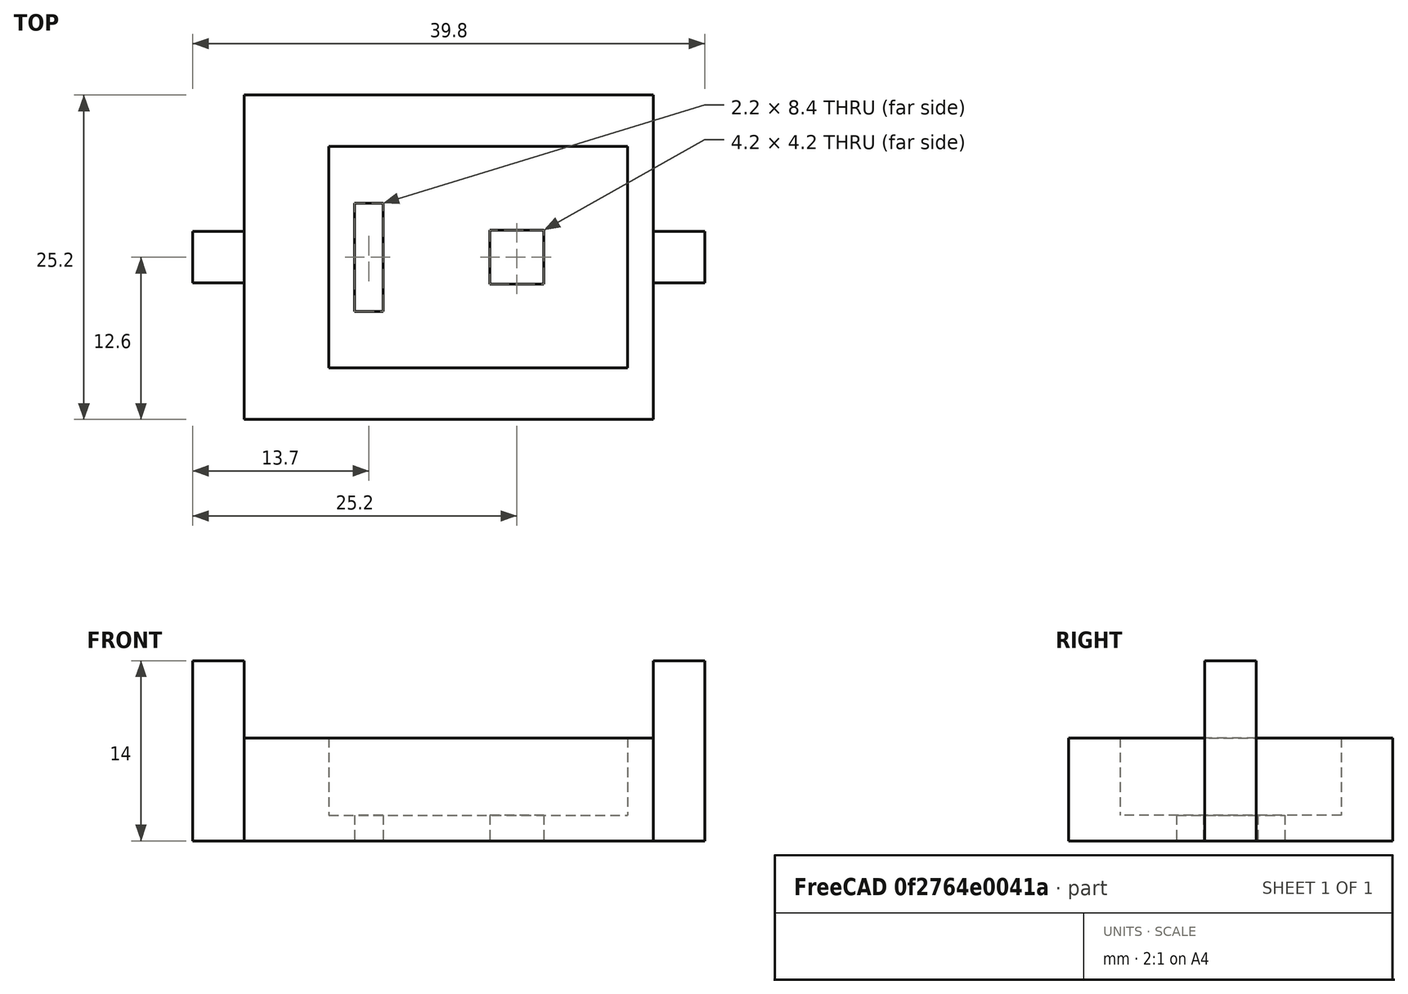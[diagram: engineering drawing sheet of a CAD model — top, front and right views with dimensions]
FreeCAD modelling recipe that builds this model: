
FCSTD DOCUMENT  (FreeCAD 0.18.1R)
Label: HeadCYL
License: All rights reserved
LicenseURL: http://en.wikipedia.org/wiki/All_rights_reserved
objects: TechDraw::DrawViewDimension×13, Sketcher::SketchObject×9, TechDraw::DrawProjGroupItem×4, PartDesign::Pad×3, PartDesign::Plane×3, PartDesign::Pocket×3, TechDraw::DrawSVGTemplate×2, TechDraw::DrawPage×2, PartDesign::Body×1, TechDraw::DrawViewPart×1, TechDraw::DrawProjGroup×1
note: 25 computed .brp shape members not serialized (recipe doc carries the construction recipe); baked Part::Feature solids carry a one-line shape summary decoded from their .brp

FEATURE [Sketcher::SketchObject] Sketch
  MapMode = 5
  Support = -> [XY_Plane]
  sketch-geometry (12):
    g0: LineSegment StartX=-4 StartY=14.6 StartZ=0 EndX=-4 EndY=10.6 EndZ=0
    g1: LineSegment StartX=-4 StartY=10.6 StartZ=0 EndX=0 EndY=10.6 EndZ=0
    g2: LineSegment StartX=0 StartY=10.6 StartZ=0 EndX=0 EndY=0 EndZ=0
    g3: LineSegment StartX=0 StartY=0 StartZ=0 EndX=31.8 EndY=0 EndZ=0
    g4: LineSegment StartX=31.8 StartY=0 StartZ=0 EndX=31.8 EndY=10.6 EndZ=0
    g5: LineSegment StartX=31.8 StartY=10.6 StartZ=0 EndX=35.8 EndY=10.6 EndZ=0
    g6: LineSegment StartX=35.8 StartY=10.6 StartZ=0 EndX=35.8 EndY=14.6 EndZ=0
    g7: LineSegment StartX=35.8 StartY=14.6 StartZ=0 EndX=31.8 EndY=14.6 EndZ=0
    g8: LineSegment StartX=31.8 StartY=14.6 StartZ=0 EndX=31.8 EndY=25.2 EndZ=0
    g9: LineSegment StartX=31.8 StartY=25.2 StartZ=0 EndX=0 EndY=25.2 EndZ=0
    g10: LineSegment StartX=0 StartY=25.2 StartZ=0 EndX=0 EndY=14.6 EndZ=0
    g11: LineSegment StartX=0 StartY=14.6 StartZ=0 EndX=-4 EndY=14.6 EndZ=0
  constraints (35):
    c: Coincident(g0,g1)
    c: Coincident(g1,g2)
    c: Coincident(g2,g3)
    c: Coincident(g3,g4)
    c: Coincident(g4,g5)
    c: Coincident(g5,g6)
    c: Coincident(g6,g7)
    c: Coincident(g7,g8)
    c: Coincident(g8,g9)
    c: Coincident(g9,g10)
    c: Coincident(g10,g11)
    c: Coincident(g11,g0)
    c: Vertical(g0)
    c: Vertical(g6)
    c: Vertical(g10)
    c: Vertical(g8)
    c: Vertical(g2)
    c: Vertical(g4)
    c: Horizontal(g11)
    c: Horizontal(g1)
    c: Horizontal(g3)
    c: Horizontal(g9)
    c: Horizontal(g7)
    c: Horizontal(g5)
    c: DistanceX(g3,g3) = 31.8
    c: Coincident(g2,g-1)
    c: DistanceY(g2,g2) = 10.6
    c: DistanceY(g10,g10) = 10.6
    c: DistanceY(g8,g8) = 10.6
    c: DistanceY(g4,g4) = 10.6
    c: DistanceX(g11,g11) = 4
    c: Equal(g11,g7)
    c: Equal(g7,g5)
    c: Equal(g5,g1)
    c: DistanceY(g0,g0) = 4
FEATURE [PartDesign::Pad] Pad
  Length = 8
  Length2 = 100
  Profile = -> Sketch
  Type = 0
FEATURE [PartDesign::Plane] DatumPlane
  Length = 53.8303
  MapMode = 5
  Placement = pos=(0,0,8) rot=(0,0,1;0rad)
  ResizeMode = 0
  Support = -> [Pad]
  Width = 43.2303
FEATURE [Sketcher::SketchObject] Sketch001
  MapMode = 5
  Placement = pos=(0,0,8) rot=(0,0,1;0rad)
  Support = -> [DatumPlane]
  sketch-geometry (4):
    g0: LineSegment StartX=3.91455 StartY=22.072 StartZ=0 EndX=27.1145 EndY=22.072 EndZ=0
    g1: LineSegment StartX=27.1145 StartY=22.072 StartZ=0 EndX=27.1145 EndY=4.87202 EndZ=0
    g2: LineSegment StartX=27.1145 StartY=4.87202 StartZ=0 EndX=3.91455 EndY=4.87202 EndZ=0
    g3: LineSegment StartX=3.91455 StartY=4.87202 StartZ=0 EndX=3.91455 EndY=22.072 EndZ=0
  constraints (10):
    c: Coincident(g0,g1)
    c: Coincident(g1,g2)
    c: Coincident(g2,g3)
    c: Coincident(g3,g0)
    c: Horizontal(g0)
    c: Horizontal(g2)
    c: Vertical(g1)
    c: Vertical(g3)
    c: DistanceX(g0,g0) = 23.2
    c: DistanceY(g3,g3) = 17.2
FEATURE [Sketcher::SketchObject] Sketch002
  MapMode = 5
  Placement = pos=(0,0,8) rot=(0,0,1;0rad)
  Support = -> [DatumPlane]
  sketch-geometry (4):
    g0: LineSegment StartX=2.87872 StartY=21.6787 StartZ=0 EndX=26.0787 EndY=21.6787 EndZ=0
    g1: LineSegment StartX=26.0787 StartY=21.6787 StartZ=0 EndX=26.0787 EndY=4.47867 EndZ=0
    g2: LineSegment StartX=26.0787 StartY=4.47867 StartZ=0 EndX=2.87872 EndY=4.47867 EndZ=0
    g3: LineSegment StartX=2.87872 StartY=4.47867 StartZ=0 EndX=2.87872 EndY=21.6787 EndZ=0
  constraints (10):
    c: Coincident(g0,g1)
    c: Coincident(g1,g2)
    c: Coincident(g2,g3)
    c: Coincident(g3,g0)
    c: Horizontal(g0)
    c: Horizontal(g2)
    c: Vertical(g1)
    c: Vertical(g3)
    c: DistanceX(g0,g0) = 23.2
    c: DistanceY(g3,g3) = 17.2
FEATURE [Sketcher::SketchObject] Sketch003
  MapMode = 5
  Placement = pos=(0,0,8) rot=(0,0,1;0rad)
  Support = -> [DatumPlane]
  sketch-geometry (4):
    g0: LineSegment StartX=6.6 StartY=21.2 StartZ=0 EndX=29.8 EndY=21.2 EndZ=0
    g1: LineSegment StartX=29.8 StartY=21.2 StartZ=0 EndX=29.8 EndY=4 EndZ=0
    g2: LineSegment StartX=29.8 StartY=4 StartZ=0 EndX=6.6 EndY=4 EndZ=0
    g3: LineSegment StartX=6.6 StartY=4 StartZ=0 EndX=6.6 EndY=21.2 EndZ=0
  constraints (12):
    c: Coincident(g0,g1)
    c: Coincident(g1,g2)
    c: Coincident(g2,g3)
    c: Coincident(g3,g0)
    c: Horizontal(g0)
    c: Horizontal(g2)
    c: Vertical(g1)
    c: Vertical(g3)
    c: DistanceX(g-1,g2) = 6.6
    c: DistanceX(g2,g2) = 23.2
    c: DistanceY(g3,g3) = 17.2
    c: DistanceY(g-1,g2) = 4
FEATURE [PartDesign::Pocket] Pocket
  BaseFeature = -> Pad
  Length = 6
  Length2 = 100
  Profile = -> Sketch003
  Type = 0
FEATURE [Sketcher::SketchObject] Sketch004
  MapMode = 5
  Placement = pos=(0,0,2) rot=(0,0,1;0rad)
  Support = -> [Pocket]
FEATURE [PartDesign::Plane] DatumPlane001
  Length = 53.8303
  MapMode = 5
  Placement = pos=(0,0,2) rot=(0,0,1;0rad)
  ResizeMode = 0
  Support = -> [Pocket]
  Width = 43.2303
FEATURE [Sketcher::SketchObject] Sketch005
  MapMode = 5
  Placement = pos=(0,0,2) rot=(0,0,1;0rad)
  Support = -> [DatumPlane001]
  sketch-geometry (4):
    g0: LineSegment StartX=8.6 StartY=16.8 StartZ=0 EndX=10.8 EndY=16.8 EndZ=0
    g1: LineSegment StartX=10.8 StartY=16.8 StartZ=0 EndX=10.8 EndY=8.4 EndZ=0
    g2: LineSegment StartX=10.8 StartY=8.4 StartZ=0 EndX=8.6 EndY=8.4 EndZ=0
    g3: LineSegment StartX=8.6 StartY=8.4 StartZ=0 EndX=8.6 EndY=16.8 EndZ=0
  constraints (12):
    c: Coincident(g0,g1)
    c: Coincident(g1,g2)
    c: Coincident(g2,g3)
    c: Coincident(g3,g0)
    c: Horizontal(g0)
    c: Horizontal(g2)
    c: Vertical(g1)
    c: Vertical(g3)
    c: DistanceY(g3,g3) = 8.4
    c: DistanceX(g0,g0) = 2.2
    c: DistanceY(g-1,g2) = 8.4
    c: DistanceX(g-1,g2) = 8.6
FEATURE [PartDesign::Pocket] Pocket001
  BaseFeature = -> Pocket
  Length = 7
  Length2 = 100
  Profile = -> Sketch005
  Type = 0
FEATURE [Sketcher::SketchObject] Sketch006
  MapMode = 5
  Placement = pos=(0,0,2) rot=(0,0,1;0rad)
  Support = -> [DatumPlane001]
  sketch-geometry (4):
    g0: LineSegment StartX=19.1 StartY=14.7 StartZ=0 EndX=23.3 EndY=14.7 EndZ=0
    g1: LineSegment StartX=23.3 StartY=14.7 StartZ=0 EndX=23.3 EndY=10.5 EndZ=0
    g2: LineSegment StartX=23.3 StartY=10.5 StartZ=0 EndX=19.1 EndY=10.5 EndZ=0
    g3: LineSegment StartX=19.1 StartY=10.5 StartZ=0 EndX=19.1 EndY=14.7 EndZ=0
  constraints (12):
    c: Coincident(g0,g1)
    c: Coincident(g1,g2)
    c: Coincident(g2,g3)
    c: Coincident(g3,g0)
    c: Horizontal(g0)
    c: Horizontal(g2)
    c: Vertical(g1)
    c: Vertical(g3)
    c: DistanceX(g0,g0) = 4.2
    c: Equal(g3,g0)
    c: DistanceY(g-1,g2) = 10.5
    c: DistanceX(g-1,g2) = 19.1
FEATURE [PartDesign::Pocket] Pocket002
  BaseFeature = -> Pocket001
  Length = 5
  Length2 = 100
  Profile = -> Sketch006
  Type = 0
FEATURE [PartDesign::Plane] DatumPlane002
  Length = 53.8303
  MapMode = 5
  Placement = pos=(0,0,8) rot=(0,0,1;0rad)
  ResizeMode = 0
  Support = -> [Pocket002]
  Width = 43.2303
FEATURE [Sketcher::SketchObject] Sketch007
  MapMode = 5
  Placement = pos=(0,0,8) rot=(0,0,1;0rad)
  Support = -> [DatumPlane002]
  sketch-geometry (4):
    g0: LineSegment StartX=-4 StartY=14.6 StartZ=0 EndX=0 EndY=14.6 EndZ=0
    g1: LineSegment StartX=0 StartY=14.6 StartZ=0 EndX=0 EndY=10.6 EndZ=0
    g2: LineSegment StartX=0 StartY=10.6 StartZ=0 EndX=-4 EndY=10.6 EndZ=0
    g3: LineSegment StartX=-4 StartY=10.6 StartZ=0 EndX=-4 EndY=14.6 EndZ=0
  constraints (12):
    c: Coincident(g0,g1)
    c: Coincident(g1,g2)
    c: Coincident(g2,g3)
    c: Coincident(g3,g0)
    c: Horizontal(g0)
    c: Horizontal(g2)
    c: Vertical(g1)
    c: Vertical(g3)
    c: DistanceX(g0,g0) = 4
    c: DistanceY(g3,g3) = 4
    c: DistanceX(g-1,g1) = 0
    c: DistanceY(g-1,g1) = 10.6
FEATURE [PartDesign::Pad] Pad001
  BaseFeature = -> Pocket002
  Length = 6
  Length2 = 100
  Profile = -> Sketch007
  Type = 0
FEATURE [Sketcher::SketchObject] Sketch008
  MapMode = 5
  Placement = pos=(0,0,8) rot=(0,0,1;0rad)
  Support = -> [DatumPlane002]
  sketch-geometry (4):
    g0: LineSegment StartX=31.8 StartY=14.6 StartZ=0 EndX=35.8 EndY=14.6 EndZ=0
    g1: LineSegment StartX=35.8 StartY=14.6 StartZ=0 EndX=35.8 EndY=10.6 EndZ=0
    g2: LineSegment StartX=35.8 StartY=10.6 StartZ=0 EndX=31.8 EndY=10.6 EndZ=0
    g3: LineSegment StartX=31.8 StartY=10.6 StartZ=0 EndX=31.8 EndY=14.6 EndZ=0
  constraints (12):
    c: Coincident(g0,g1)
    c: Coincident(g1,g2)
    c: Coincident(g2,g3)
    c: Coincident(g3,g0)
    c: Horizontal(g0)
    c: Horizontal(g2)
    c: Vertical(g1)
    c: Vertical(g3)
    c: DistanceX(g0,g0) = 4
    c: DistanceY(g3,g3) = 4
    c: DistanceX(g-1,g2) = 31.8
    c: DistanceY(g-1,g2) = 10.6
FEATURE [PartDesign::Pad] Pad002
  BaseFeature = -> Pad001
  Length = 6
  Length2 = 100
  Profile = -> Sketch008
  Type = 0
FEATURE [PartDesign::Body] Body
  Group = -> [Sketch,Pad,DatumPlane,Sketch001,Sketch002,Sketch003,Pocket,Sketch004,DatumPlane001,Sketch005,Pocket001,Sketch006,Pocket002,DatumPlane002,Sketch007,Pad001,Sketch008,Pad002]
  Origin = -> Origin
  Tip = -> Pad002
FEATURE [TechDraw::DrawSVGTemplate] Template
  EditableTexts = Designed_by_Name=Designed by Name; Drawing_number=Drawing number; FC-Date=Date; FC-SC=Scale; FC-SH=Sheet; FC-Title=Title; Subtitle=Subtitle; Weight=Weight
  Height = 210
  Orientation = 1
  Width = 297
FEATURE [TechDraw::DrawViewPart] View
  CoarseView = false
  Direction = (0,-1,0)
  Focus = 100
  HardHidden = false
  IsoCount = 0
  IsoHidden = false
  IsoVisible = false
  LockPosition = false
  Perspective = false
  Rotation = 0
  ScaleType = 0
  SeamHidden = false
  SeamVisible = false
  SmoothHidden = false
  SmoothVisible = false
  Source = -> [Body]
  X = 148.5
  Y = 105
FEATURE [TechDraw::DrawPage] Page
  KeepUpdated = true
  ProjectionType = 0
  Template = -> Template
  Views = -> [View]
FEATURE [TechDraw::DrawSVGTemplate] Template001
  EditableTexts = Approved1=Approved 1; Approved2=Approved 2; CheckedBy=Checked By; Code=Code; CompanyAddress=1234 Main St; CompanyName=Company Name; DrawingNumber=Drawing Number; DrawingTitle1=Drawing Title 1; DrawingTitle2=Drawing Title 2; DrawingTitle3=Drawing Title 3; DrawnBy=Drawn By; Revision=Rev; Scale=Scale; Sheet=Sheet n of m; Weight=Weight
  Height = 279.4
  Orientation = 1
  Width = 431.8
FEATURE [TechDraw::DrawProjGroupItem] ProjItem  label="Front"
  CoarseView = false
  Direction = (0,-1,0)
  Focus = 100
  HardHidden = false
  IsoCount = 0
  IsoHidden = false
  IsoVisible = false
  LockPosition = true
  Perspective = false
  Rotation = 0
  RotationVector = (1,0,0)
  Scale = 2
  ScaleType = 2
  SeamHidden = false
  SeamVisible = false
  SmoothHidden = false
  SmoothVisible = false
  Source = -> [Body]
  Type = 0
  X = 0
  Y = 0
FEATURE [TechDraw::DrawProjGroupItem] ProjItem001  label="Left"
  CoarseView = false
  Direction = (-1,-1e-16,0)
  Focus = 100
  HardHidden = false
  IsoCount = 0
  IsoHidden = false
  IsoVisible = false
  LockPosition = false
  Perspective = false
  Rotation = 0
  RotationVector = (1e-16,-1,0)
  Scale = 2
  ScaleType = 2
  SeamHidden = false
  SeamVisible = false
  SmoothHidden = false
  SmoothVisible = false
  Source = -> [Body]
  Type = 1
  X = 95.6102
  Y = 0
FEATURE [TechDraw::DrawProjGroupItem] ProjItem002  label="FrontTopLeft"
  CoarseView = false
  Direction = (-1,-1,1)
  Focus = 100
  HardHidden = false
  IsoCount = 0
  IsoHidden = false
  IsoVisible = false
  LockPosition = false
  Perspective = false
  Rotation = 0
  RotationVector = (1,-1,0)
  Scale = 2
  ScaleType = 2
  SeamHidden = false
  SeamVisible = false
  SmoothHidden = false
  SmoothVisible = false
  Source = -> [Body]
  Type = 6
  X = 95.6102
  Y = -95.6102
FEATURE [TechDraw::DrawProjGroupItem] ProjItem003  label="Top"
  CoarseView = false
  Direction = (0,0,1)
  Focus = 100
  HardHidden = false
  IsoCount = 0
  IsoHidden = false
  IsoVisible = false
  LockPosition = false
  Perspective = false
  Rotation = 0
  RotationVector = (1,0,0)
  Scale = 2
  ScaleType = 2
  SeamHidden = false
  SeamVisible = false
  SmoothHidden = false
  SmoothVisible = false
  Source = -> [Body]
  Type = 4
  X = 0
  Y = -95.6102
FEATURE [TechDraw::DrawProjGroup] ProjGroup
  Anchor = -> ProjItem
  AutoDistribute = true
  LockPosition = false
  ProjectionType = 0
  Rotation = 0
  Scale = 2
  ScaleType = 2
  Source = -> [Body]
  Views = -> [ProjItem,ProjItem001,ProjItem002,ProjItem003]
  X = 98.093
  Y = 193.436
  spacingX = 15
  spacingY = 15
FEATURE [TechDraw::DrawViewDimension] Dimension
  Arbitrary = false
  FormatSpec = %.4f
  LockPosition = false
  MeasureType = 1
  OverTolerance = 0
  References2D = -> [ProjItem]
  Rotation = 0
  ScaleType = 0
  Type = 1
  UnderTolerance = 0
  X = 1.24312
  Y = -26.4312
FEATURE [TechDraw::DrawViewDimension] Dimension001
  Arbitrary = false
  FormatSpec = %.4f
  LockPosition = false
  MeasureType = 1
  OverTolerance = 0
  References2D = -> [ProjItem]
  Rotation = 0
  ScaleType = 0
  Type = 1
  UnderTolerance = 0
  X = -34.8677
  Y = 25.8097
FEATURE [TechDraw::DrawViewDimension] Dimension002
  Arbitrary = false
  FormatSpec = %.4f
  LockPosition = false
  MeasureType = 1
  OverTolerance = 0
  References2D = -> [ProjItem]
  Rotation = 0
  ScaleType = 0
  Type = 2
  UnderTolerance = 0
  X = -51.2989
  Y = -1.24312
FEATURE [TechDraw::DrawViewDimension] Dimension003
  Arbitrary = false
  FormatSpec = %.4f
  LockPosition = false
  MeasureType = 1
  OverTolerance = 0
  References2D = -> [ProjItem001]
  Rotation = 0
  ScaleType = 0
  Type = 1
  UnderTolerance = 0
  X = 0
  Y = -25.1881
FEATURE [TechDraw::DrawViewDimension] Dimension004
  Arbitrary = false
  FormatSpec = %.4f
  LockPosition = false
  MeasureType = 1
  OverTolerance = 0
  References2D = -> [ProjItem001]
  Rotation = 0
  ScaleType = 0
  Type = 1
  UnderTolerance = 0
  X = 1.86468
  Y = 25.8097
FEATURE [TechDraw::DrawViewDimension] Dimension005
  Arbitrary = false
  FormatSpec = %.4f
  LockPosition = false
  MeasureType = 1
  OverTolerance = 0
  References2D = -> [ProjItem001]
  Rotation = 0
  ScaleType = 0
  Type = 2
  UnderTolerance = 0
  X = 35.4558
  Y = -6.62156
FEATURE [TechDraw::DrawViewDimension] Dimension006
  Arbitrary = false
  FormatSpec = %.4f
  LockPosition = false
  MeasureType = 1
  OverTolerance = 0
  References2D = -> [ProjItem003]
  Rotation = 0
  ScaleType = 0
  Type = 1
  UnderTolerance = 0
  X = -0.310781
  Y = 40.4283
FEATURE [TechDraw::DrawViewDimension] Dimension007
  Arbitrary = false
  FormatSpec = %.4f
  LockPosition = false
  MeasureType = 1
  OverTolerance = 0
  References2D = -> [ProjItem003]
  Rotation = 0
  ScaleType = 0
  Type = 2
  UnderTolerance = 0
  X = -47.8803
  Y = -0.310781
FEATURE [TechDraw::DrawViewDimension] Dimension008
  Arbitrary = false
  FormatSpec = %.4f
  LockPosition = false
  MeasureType = 1
  OverTolerance = 0
  References2D = -> [ProjItem003]
  Rotation = 0
  ScaleType = 0
  Type = 2
  UnderTolerance = 0
  X = -53.8654
  Y = -0.932342
FEATURE [TechDraw::DrawViewDimension] Dimension009
  Arbitrary = false
  FormatSpec = %.4f
  LockPosition = false
  MeasureType = 1
  OverTolerance = 0
  References2D = -> [ProjItem003]
  Rotation = 0
  ScaleType = 0
  Type = 1
  UnderTolerance = 0
  X = 4.6
  Y = -19.3755
FEATURE [TechDraw::DrawViewDimension] Dimension010
  Arbitrary = false
  FormatSpec = %.4f
  LockPosition = false
  MeasureType = 1
  OverTolerance = 0
  References2D = -> [ProjItem003]
  Rotation = 0
  ScaleType = 0
  Type = 1
  UnderTolerance = 0
  X = -6.49517
  Y = -12.1294
FEATURE [TechDraw::DrawViewDimension] Dimension011
  Arbitrary = false
  FormatSpec = %.4f
  LockPosition = false
  MeasureType = 1
  OverTolerance = 0
  References2D = -> [ProjItem003]
  Rotation = 0
  ScaleType = 0
  Type = 2
  UnderTolerance = 0
  X = -6.18621
  Y = 0.824752
FEATURE [TechDraw::DrawViewDimension] Dimension012
  Arbitrary = false
  FormatSpec = %.4f
  LockPosition = false
  MeasureType = 1
  OverTolerance = 0
  References2D = -> [ProjItem003]
  Rotation = 0
  ScaleType = 0
  Type = 1
  UnderTolerance = 0
  X = 11.1782
  Y = 17.6436
FEATURE [TechDraw::DrawPage] Page001
  KeepUpdated = true
  ProjectionType = 0
  Template = -> Template001
  Views = -> [ProjGroup,Dimension,Dimension001,Dimension002,Dimension003,Dimension004,Dimension005,Dimension006,Dimension007,Dimension008,Dimension009,Dimension010,Dimension011,Dimension012]
